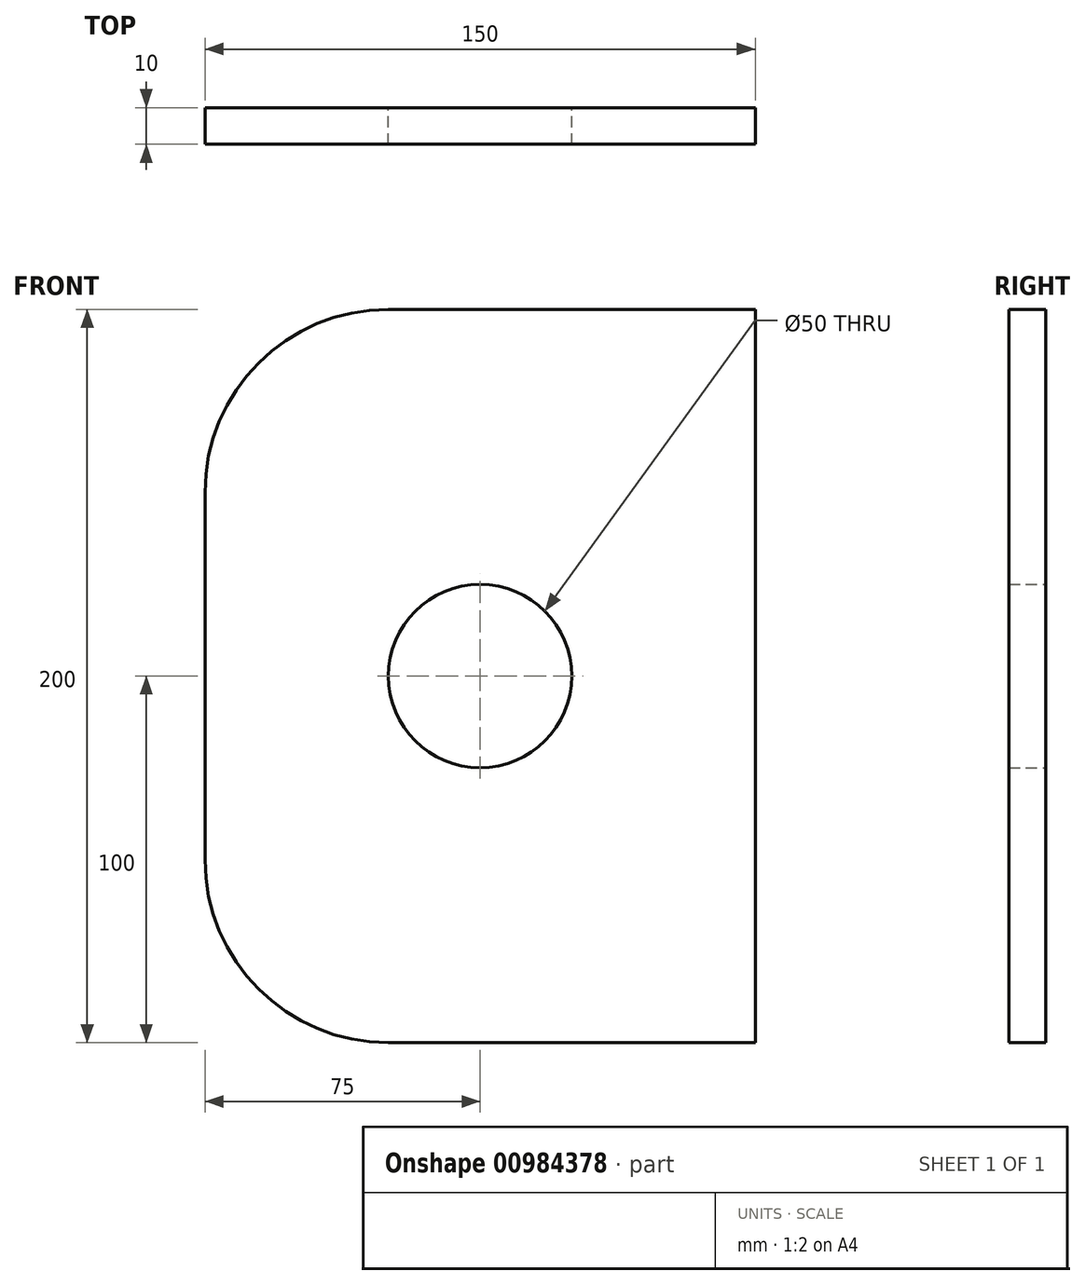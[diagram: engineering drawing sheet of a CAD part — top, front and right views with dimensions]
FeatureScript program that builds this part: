
annotation { "Feature Type Name" : "Feature", "Feature Type Description" : "" }
export const myFeature = defineFeature(function(context is Context, id is Id, definition is map)
    precondition{}
    {
        {
            var Q0;
            Q0=qCreatedBy(makeId("Front.planeOp"),FACE);
            var sketch = newSketch(context, id + "F0", { "sketchPlane" : qUnion([Q0])});
            skLineSegment(sketch, "E0.bottom", {"start": v(75, -100) * mm, "end": v(-75, -100) * mm});
            skLineSegment(sketch, "E0.top", {"start": v(75, 100) * mm, "end": v(-75, 100) * mm});
            skLineSegment(sketch, "E0.left", {"start": v(75, -100) * mm, "end": v(75, 100) * mm});
            skLineSegment(sketch, "E0.right", {"start": v(-75, -100) * mm, "end": v(-75, 100) * mm});
            skPoint(sketch, "E0.middle", {"position": v(0, 0) * mm});
            skSolve(sketch);
        }
        {
            var Q0;
            Q0=qSketchRegion(id+"F0",true);
            extrude(context, id + "F1", {"entities" : qUnion([Q0]), "depth" : 10 * mm, "offsetDistance" : 25 * mm});
        }
        {
            var Q0;
            Q0=makeQuery(id+"F1.opExtrude","SWEPT_EDGE",EDGE,{"disambiguationData":[OSD([sQuery(id+"F0.wireOp",EDGE,"E0.top"),sQuery(id+"F0.wireOp",EDGE,"E0.right")])]});
            var Q1;
            Q1=makeQuery(id+"F1.opExtrude","SWEPT_EDGE",EDGE,{"disambiguationData":[OSD([sQuery(id+"F0.wireOp",EDGE,"E0.bottom"),sQuery(id+"F0.wireOp",EDGE,"E0.right")])]});
            fillet(context, id + "F2", {"entities" : qUnion([Q0, Q1]), "radius" : 50 * mm, "tangentPropagation" : true, "allowEdgeOverflow" : false});
        }
        {
            var Q0;
            Q0=qCreatedBy(makeId("Front.planeOp"),FACE);
            var sketch = newSketch(context, id + "F3", { "sketchPlane" : qUnion([Q0])});
            skCircle(sketch, "E1", {"center": v(0, 0) * mm, "radius": 25 * mm});
            skSolve(sketch);
        }
        {
            var Q0;
            Q0=sQuery(id+"F3.wireOp",VERTEX,"E1.center");
            var Q1;
            Q1=makeQuery(id+"F1.opExtrude","SWEPT_BODY",BODY,{"disambiguationData":[OSD([sQuery(id+"F0.wireOp",EDGE,"E0.bottom"),sQuery(id+"F0.wireOp",EDGE,"E0.top"),sQuery(id+"F0.wireOp",EDGE,"E0.left"),sQuery(id+"F0.wireOp",EDGE,"E0.right")])]});
            hole(context, id + "F4", {"style" : HoleStyle.SIMPLE, "endStyle" : HoleEndStyle.THROUGH, "oppositeDirection" : true, "holeDiameter" : 50 * mm, "majorDiameter" : 5 * mm, "isTappedThrough" : true, "tappedDepth" : 12 * mm, "tapClearance" : 3, "locations" : qUnion([Q0]), "scope" : qUnion([Q1])});
        }
    });
